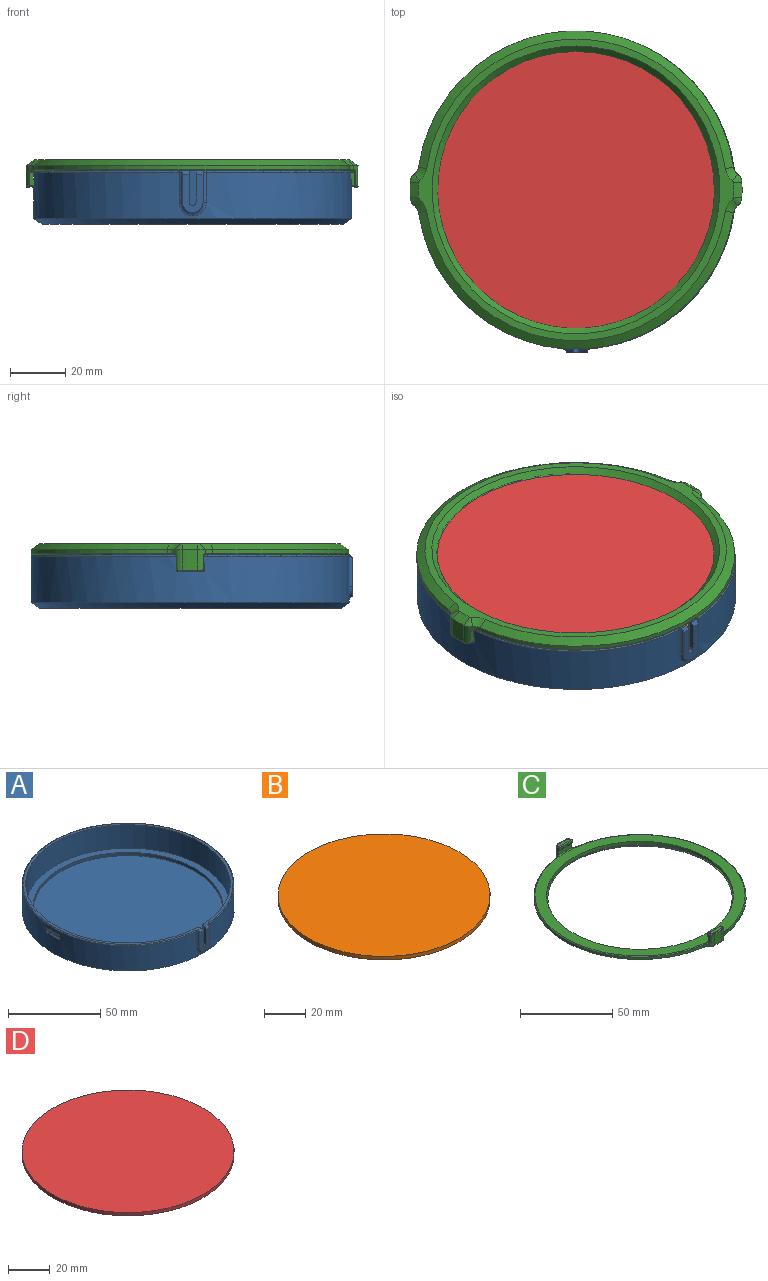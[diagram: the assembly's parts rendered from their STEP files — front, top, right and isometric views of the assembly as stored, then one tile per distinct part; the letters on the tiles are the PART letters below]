
ASSEMBLY  parts=4 mates=4
PART A: 37 faces, bbox 124.6x124.4x20.6 mm
  f0: cylinder r=3.75mm len=3.75mm, axis (0,1,0), area 0.6mm2, adj f21,f23,f29
  f1: torus R=57mm, axis (0,0,1), area 275.1mm2, adj f2,f4,f27,f31
  f2: cylinder r=57.5mm len=115mm, axis (0,0,-1), area 5828.6mm2, adj f1,f9,f10,f12,f13,f14,f15,f17
  f3: cylinder r=55.5mm len=111mm, axis (0,0,1), area 5355.4mm2, adj f4,f5,f34,f35,f36
  f4: plane 114.61x114.11mm, normal (0,0,1), area 529.8mm2, adj f1,f3,f24,f26,f27,f31,f32,f33
  f5: plane 111x111mm, normal (0,0,1), area 1344.6mm2, adj f3,f6
  f6: cylinder r=51.5mm len=103mm, axis (0,0,-1), area 679.5mm2, adj f5,f7
  f7: plane 103x103mm, normal (0,0,1), area 8332.3mm2, adj f6
  f8: plane 109x109mm, normal (0,0,-1), area 9331.3mm2, adj f19
  f9: plane 3x0.6mm, normal (0,1,0), area 1.2mm2, adj f2,f11,f12,f13
  f10: plane 3x0.6mm, normal (0,-1,0), area 1.2mm2, adj f2,f11,f12,f13
  f11: bspline ~10.05x1mm, area 10.1mm2, adj f9,f10,f12,f13
  f12: bspline ~10.05x0.89mm, area 8.4mm2, adj f2,f9,f10,f11
  f13: bspline ~10.05x1.43mm, area 15.6mm2, adj f2,f9,f10,f11
  f14: plane 3x0.6mm, normal (0,1,0), area 1.2mm2, adj f2,f16,f17,f18
  f15: plane 3x0.6mm, normal (0,-1,0), area 1.2mm2, adj f2,f16,f17,f18
  f16: bspline ~10.05x1mm, area 10.1mm2, adj f14,f15,f17,f18
  f17: bspline ~10.05x0.89mm, area 8.4mm2, adj f2,f14,f15,f16
  f18: bspline ~10.05x1.43mm, area 15.6mm2, adj f2,f14,f15,f16
  f19: cone r=57.5mm half-angle=56.3deg, axis (0,0,1), area 1268.6mm2, adj f2,f8
  f20: cylinder r=3.75mm len=3.75mm, axis (0,1,0), area 0.6mm2, adj f22,f23,f29
  f21: plane 10.21x0.21mm, normal (-1,0,0), area 2.2mm2, adj f0,f23,f30,f32
  f22: plane 10.21x0.21mm, normal (1,0,0), area 2.2mm2, adj f20,f23,f28,f33
  f23: plane 13.75x7.5mm, normal (0,-1,0), area 69.6mm2, adj f0,f20,f21,f22,f24,f25,f26,f32
  f24: plane 11.25x2.3mm, normal (1,0,0), area 25mm2, adj f4,f23,f25,f32,f34
  f25: cylinder r=1.25mm len=2.5mm, axis (0,-1,0), area 9mm2, adj f23,f24,f26,f35
  f26: plane 11.25x2.3mm, normal (-1,0,0), area 25mm2, adj f4,f23,f25,f33,f36
  f27: bspline ~2.05x2mm, area 0.7mm2, adj f1,f4,f28,f33
  f28: cylinder r=1.25mm len=10.75mm, axis (0,0,-1), area 19.8mm2, adj f2,f22,f27,f29,f33
  f29: bspline ~9.79x6.12mm, area 25.1mm2, adj f0,f2,f20,f28,f30
  f30: cylinder r=1.25mm len=10.75mm, axis (0,0,-1), area 19.8mm2, adj f2,f21,f29,f31,f32
  f31: bspline ~2.05x2mm, area 0.7mm2, adj f1,f4,f30,f32
  f32: plane 3.01x1.4mm, normal (0,-0.71,0.71), area 4.6mm2, adj f4,f21,f23,f24,f30,f31
  f33: plane 3.01x1.4mm, normal (0,-0.71,0.71), area 4.6mm2, adj f4,f22,f23,f26,f27,f28
  f34: cylinder r=1mm len=11.25mm, axis (0,0,1), area 17.2mm2, adj f3,f4,f24,f35
  f35: bspline ~4.42x2.76mm, area 7.8mm2, adj f3,f25,f34,f36
  f36: cylinder r=1mm len=11.25mm, axis (0,0,1), area 17.2mm2, adj f3,f4,f26,f35
PART B: 3 faces, bbox 102.3x102.3x2.1 mm
  f0: cylinder r=51.15mm len=102.3mm, axis (0,0,-1), area 674.9mm2, adj f1,f2
  f1: plane 102.3x102.3mm, normal (0,0,1), area 8219.4mm2, adj f0
  f2: plane 102.3x102.3mm, normal (0,0,-1), area 8219.4mm2, adj f0
PART C: 87 faces, bbox 124.6x123.3x10.7 mm
  f0: bspline ~10x0.89mm, area 7.8mm2, adj f9,f10,f17,f59,f60,f61
  f1: plane 7.78x0.52mm, normal (0,0,1), area 2.7mm2, adj f58,f67,f68,f69,f70,f71
  f2: cylinder r=57.5mm len=10mm, axis (0,0,-1), area 25mm2, adj f9,f10,f18,f27
  f3: cylinder r=57.5mm len=113.84mm, axis (0,0,-1), area 246.4mm2, adj f22,f25,f43,f57
  f4: cylinder r=57.5mm len=113.84mm, axis (0,0,-1), area 246.4mm2, adj f23,f24,f38,f46
  f5: plane 115.6x114mm, normal (0,0,1), area 2135mm2, adj f7,f26,f27,f28,f29,f30,f31,f37
  f6: plane 113.98x109mm, normal (0,0,-1), area 880.5mm2, adj f46,f47,f48,f49,f50,f51,f52,f53
  f7: cylinder r=50.7mm len=101.4mm, axis (0,0,1), area 637.1mm2, adj f5,f8
  f8: plane 101.4x101.4mm, normal (0,0,1), area 221.5mm2, adj f7,f86
  f9: plane 5.14x2.15mm, normal (-1,0,0), area 8.5mm2, adj f0,f2,f17,f18,f26,f61,f76
  f10: plane 5.14x2.15mm, normal (1,0,0), area 8.5mm2, adj f0,f2,f17,f18,f28,f60,f84
  f11: cylinder r=59.99mm len=7.5mm, axis (0,0,-1), area 41.7mm2, adj f32,f33,f51,f80
  f12: plane 7.78x0.52mm, normal (0,0,1), area 2.7mm2, adj f59,f78,f79,f80,f81,f82
  f13: cylinder r=57.5mm len=10mm, axis (0,0,-1), area 25mm2, adj f14,f15,f20,f30
  f14: plane 5.14x2.15mm, normal (1,0,0), area 8.5mm2, adj f13,f19,f20,f21,f29,f62,f65
  f15: plane 5.14x2.15mm, normal (-1,0,0), area 8.5mm2, adj f13,f19,f20,f21,f31,f63,f73
  f16: cylinder r=59.99mm len=7.5mm, axis (0,0,-1), area 41.7mm2, adj f34,f35,f52,f69
  f17: bspline ~10x1mm, area 10mm2, adj f0,f9,f10,f18
  f18: bspline ~10x1.43mm, area 15.5mm2, adj f2,f9,f10,f17
  f19: bspline ~10x1mm, area 10mm2, adj f14,f15,f20,f21
  f20: bspline ~10x1.43mm, area 15.5mm2, adj f13,f14,f15,f19
  f21: bspline ~10x0.89mm, area 7.8mm2, adj f14,f15,f19,f58,f62,f63
  f22: cylinder r=3.8mm len=2.51mm, axis (0,0,1), area 4.5mm2, adj f3,f35,f41,f42,f56
  f23: cylinder r=3.8mm len=2.51mm, axis (0,0,1), area 4.5mm2, adj f4,f34,f39,f40,f48
  f24: cylinder r=3.8mm len=2.51mm, axis (0,0,1), area 4.5mm2, adj f4,f33,f36,f37,f47
  f25: cylinder r=3.8mm len=2.51mm, axis (0,0,1), area 4.5mm2, adj f3,f32,f44,f45,f55
  f26: cylinder r=0.5mm len=2.1mm, axis (0,-1,0), area 1.1mm2, adj f5,f9,f27,f36,f75
  f27: torus R=57mm, axis (0,0,1), area 8.3mm2, adj f2,f5,f26,f28
  f28: cylinder r=0.5mm len=2.1mm, axis (0,-1,0), area 1.1mm2, adj f5,f10,f27,f45,f85
  f29: cylinder r=0.5mm len=2.1mm, axis (0,1,0), area 1.1mm2, adj f5,f14,f30,f41,f64
  f30: torus R=57mm, axis (0,0,1), area 8.3mm2, adj f5,f13,f29,f31
  f31: cylinder r=0.5mm len=2.1mm, axis (0,1,0), area 1.1mm2, adj f5,f15,f30,f40,f74
  f32: cylinder r=3.8mm len=7.5mm, axis (0,0,1), area 18.5mm2, adj f11,f25,f53,f81,f82,f84,f85
  f33: cylinder r=3.8mm len=7.5mm, axis (0,0,1), area 18.5mm2, adj f11,f24,f49,f75,f76,f78,f79
  f34: cylinder r=3.8mm len=7.5mm, axis (0,0,1), area 18.5mm2, adj f16,f23,f50,f70,f71,f73,f74
  f35: cylinder r=3.8mm len=7.5mm, axis (0,0,1), area 18.5mm2, adj f16,f22,f54,f64,f65,f67,f68
  f36: bspline ~1x0.68mm, area 0.2mm2, adj f24,f26,f37,f75
  f37: torus R=4.3mm, axis (0,0,1), area 2.2mm2, adj f5,f24,f36,f38
  f38: torus R=57mm, axis (0,0,1), area 128.6mm2, adj f4,f5,f37,f39
  f39: torus R=4.3mm, axis (0,0,1), area 2.2mm2, adj f5,f23,f38,f40
  f40: bspline ~1x0.68mm, area 0.2mm2, adj f23,f31,f39,f74
  f41: bspline ~1x0.68mm, area 0.2mm2, adj f22,f29,f42,f64
  f42: torus R=4.3mm, axis (0,0,1), area 2.2mm2, adj f5,f22,f41,f43
  f43: torus R=57mm, axis (0,0,1), area 128.6mm2, adj f3,f5,f42,f44
  f44: torus R=4.3mm, axis (0,0,1), area 2.2mm2, adj f5,f25,f43,f45
  f45: bspline ~1x0.68mm, area 0.2mm2, adj f25,f28,f44,f85
  f46: cone r=57.5mm half-angle=56.3deg, axis (0,0,1), area 576.9mm2, adj f4,f6,f47,f48
  f47: cone r=6.8mm half-angle=56.3deg, axis (0,0,-1), area 15mm2, adj f6,f24,f46,f49
  f48: cone r=6.8mm half-angle=56.3deg, axis (0,0,-1), area 15mm2, adj f6,f23,f46,f50
  f49: cone r=0.8mm half-angle=56.3deg, axis (0,0,1), area 7.3mm2, adj f6,f33,f47,f51
  f50: cone r=0.8mm half-angle=56.3deg, axis (0,0,1), area 7.3mm2, adj f6,f34,f48,f52
  f51: cone r=56.99mm half-angle=56.3deg, axis (0,0,1), area 19.6mm2, adj f6,f11,f49,f53
  f52: cone r=56.99mm half-angle=56.3deg, axis (0,0,1), area 19.6mm2, adj f6,f16,f50,f54
  f53: cone r=0.8mm half-angle=56.3deg, axis (0,0,1), area 7.3mm2, adj f6,f32,f51,f55
  f54: cone r=0.8mm half-angle=56.3deg, axis (0,0,1), area 7.3mm2, adj f6,f35,f52,f56
  f55: cone r=6.8mm half-angle=56.3deg, axis (0,0,-1), area 15mm2, adj f6,f25,f53,f57
  f56: cone r=6.8mm half-angle=56.3deg, axis (0,0,-1), area 15mm2, adj f6,f22,f54,f57
  f57: cone r=57.5mm half-angle=56.3deg, axis (0,0,1), area 576.9mm2, adj f3,f6,f55,f56
  f58: cylinder r=1.74mm len=9mm, axis (-1,0,0), area 15.5mm2, adj f1,f21,f62,f63,f67,f71
  f59: cylinder r=1.74mm len=9mm, axis (-1,0,0), area 15.5mm2, adj f0,f12,f60,f61,f78,f82
  f60: torus R=2.24mm, axis (1,0,0), area 1.3mm2, adj f0,f10,f59,f83
  f61: torus R=2.24mm, axis (1,0,0), area 1.3mm2, adj f0,f9,f59,f77
  f62: torus R=2.24mm, axis (-1,0,0), area 1.3mm2, adj f14,f21,f58,f66
  f63: torus R=2.24mm, axis (-1,0,0), area 1.3mm2, adj f15,f21,f58,f72
  f64: bspline ~1.56x1.19mm, area 0.7mm2, adj f29,f35,f41,f65
  f65: cylinder r=0.5mm len=4.85mm, axis (0,0,1), area 2.3mm2, adj f14,f35,f64,f66
  f66: sphere r=0.5mm, area 0.3mm2, adj f62,f65,f67
  f67: bspline ~2.5x1.54mm, area 0.9mm2, adj f1,f35,f58,f66,f68
  f68: torus R=3.3mm, axis (0,0,-1), area 0.9mm2, adj f1,f35,f67,f69
  f69: torus R=59.49mm, axis (0,0,-1), area 4.4mm2, adj f1,f16,f68,f70
  f70: torus R=3.3mm, axis (0,0,-1), area 0.9mm2, adj f1,f34,f69,f71
  f71: bspline ~2.5x1.54mm, area 0.9mm2, adj f1,f34,f58,f70,f72
  f72: sphere r=0.5mm, area 0.3mm2, adj f63,f71,f73
  f73: cylinder r=0.5mm len=4.85mm, axis (0,0,1), area 2.3mm2, adj f15,f34,f72,f74
  f74: bspline ~1.56x1.18mm, area 0.7mm2, adj f31,f34,f40,f73
  f75: bspline ~1.56x1.19mm, area 0.7mm2, adj f26,f33,f36,f76
  f76: cylinder r=0.5mm len=4.85mm, axis (0,0,1), area 2.3mm2, adj f9,f33,f75,f77
  f77: sphere r=0.5mm, area 0.3mm2, adj f61,f76,f78
  f78: bspline ~2.5x1.54mm, area 0.9mm2, adj f12,f33,f59,f77,f79
  f79: torus R=3.3mm, axis (0,0,-1), area 0.9mm2, adj f12,f33,f78,f80
  f80: torus R=59.49mm, axis (0,0,-1), area 4.4mm2, adj f11,f12,f79,f81
  f81: torus R=3.3mm, axis (0,0,-1), area 0.9mm2, adj f12,f32,f80,f82
  f82: bspline ~2.5x1.54mm, area 0.9mm2, adj f12,f32,f59,f81,f83
  f83: sphere r=0.5mm, area 0.3mm2, adj f60,f82,f84
  f84: cylinder r=0.5mm len=4.85mm, axis (0,0,1), area 2.3mm2, adj f10,f32,f83,f85
  f85: bspline ~1.56x1.18mm, area 0.7mm2, adj f28,f32,f45,f84
  f86: cone r=50mm half-angle=45deg, axis (0,0,-1), area 906.3mm2, adj f6,f8
PART D: 3 faces, bbox 101.3x101.3x1.9 mm
  f0: cylinder r=50.65mm len=101.3mm, axis (0,0,-1), area 604.7mm2, adj f1,f2
  f1: plane 101.3x101.3mm, normal (0,0,1), area 8059.5mm2, adj f0
  f2: plane 101.3x101.3mm, normal (0,0,-1), area 8059.5mm2, adj f0
PLACE A t=(1.85,-2.53,2.69)mm
PLACE B t=(1.85,-2.53,4.29)mm
PLACE C rot(axis=(0.71,0.71,0),180deg) t=(1.61,-2.4,25.89)mm
PLACE D rot(axis=(0,0,1),17.2deg) t=(1.85,-2.53,22.06)mm
MATE cylindrical A.f6 <-> B.f0  axis (0,0,1) through (1.85,-2.53,4.29)mm
MATE planar C.f86 <-> A.f4  axis (0,0,-1) through (1.61,-2.4,21.89)mm
MATE planar B.f0 <-> A.f6  axis (0,0,-1) through (1.85,-2.53,4.29)mm
MATE cylindrical D.f0 <-> A.f6  axis (0,0,-1) through (1.85,-2.53,22.06)mm
